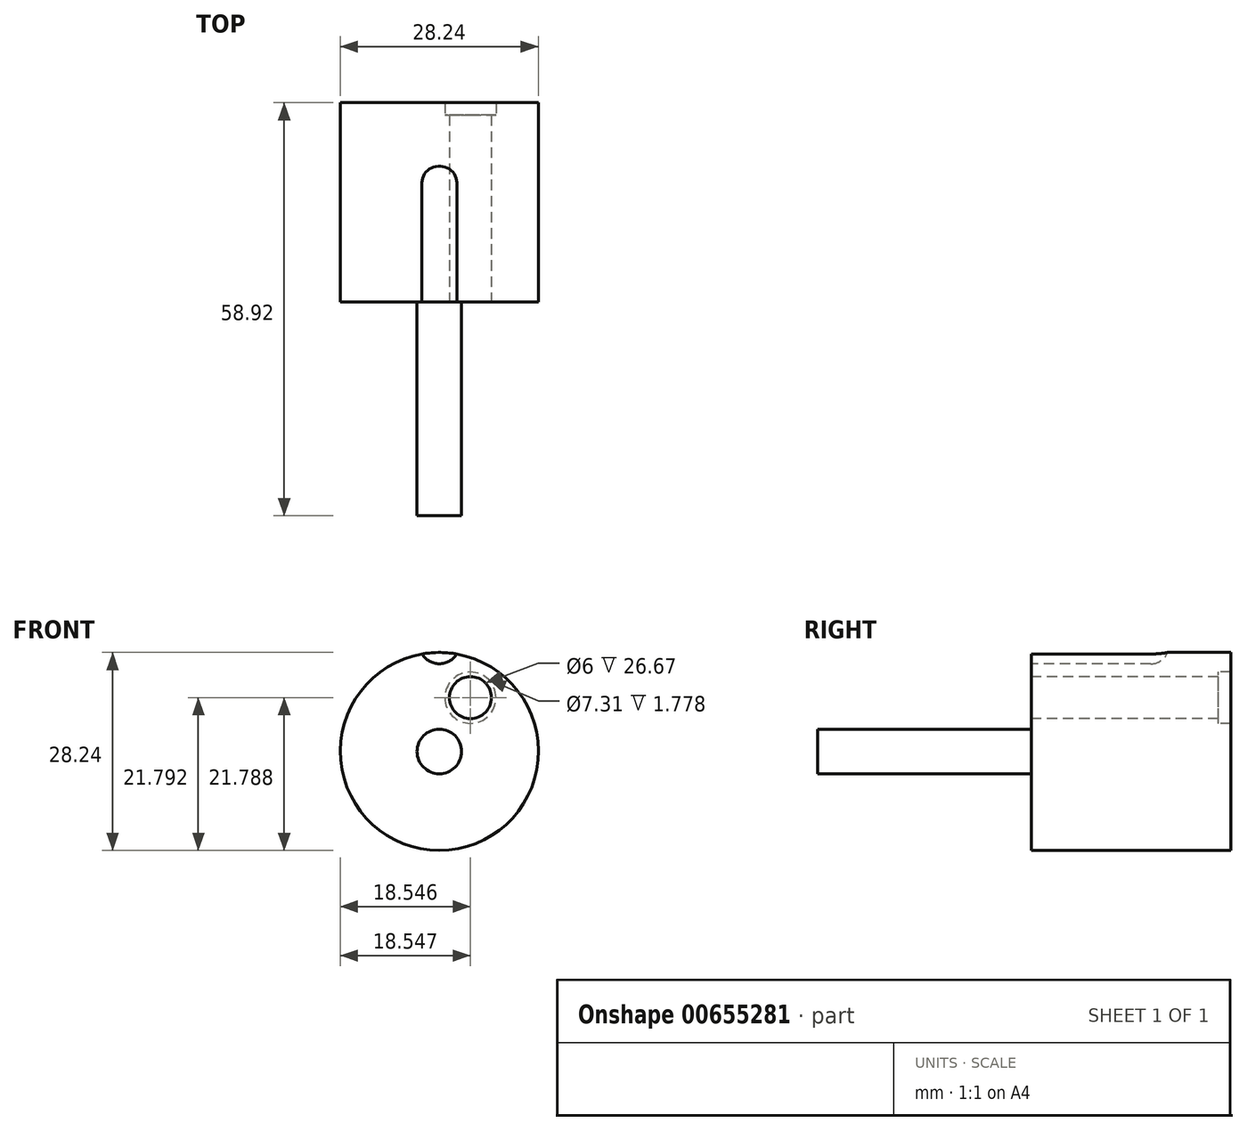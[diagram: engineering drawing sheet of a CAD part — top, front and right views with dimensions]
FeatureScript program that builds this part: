
annotation { "Feature Type Name" : "Feature", "Feature Type Description" : "" }
export const myFeature = defineFeature(function(context is Context, id is Id, definition is map)
    precondition{}
    {
        {
            var Q0;
            Q0=qCreatedBy(makeId("Front.planeOp"),FACE);
            var sketch = newSketch(context, id + "F0", { "sketchPlane" : qUnion([Q0])});
            skCircle(sketch, "E0", {"center": v(0, 0) * mm, "radius": 14.12 * mm});
            skSolve(sketch);
        }
        {
            var Q0;
            Q0=qSketchRegion(id+"F0",true);
            extrude(context, id + "F1", {"entities" : qUnion([Q0]), "endBound" : BoundingType.SYMMETRIC, "depth" : 28.45 * mm, "offsetDistance" : 25.4 * mm});
        }
        {
            var Q0;
            Q0=qCreatedBy(makeId("Front.planeOp"),FACE);
            var sketch = newSketch(context, id + "F2", { "sketchPlane" : qUnion([Q0])});
            skCircle(sketch, "E1", {"center": v(0, 0) * mm, "radius": 3.18 * mm});
            skSolve(sketch);
        }
        {
            var Q0;
            Q0=qSketchRegion(id+"F2",true);
            extrude(context, id + "F3", {"entities" : qUnion([Q0]), "operationType" : NewBodyOperationType.ADD, "depth" : 44.7 * mm, "offsetDistance" : 25.4 * mm});
        }
        {
            var Q0;
            Q0=makeQuery(id+"F1.opExtrude","CAP_FACE",FACE,{"disambiguationData":[OSD([sQuery(id+"F0.wireOp",EDGE,"E0")])],"isStart":false});
            var sketch = newSketch(context, id + "F4", { "sketchPlane" : qUnion([Q0])});
            skCircle(sketch, "E2", {"center": v(0, 15.4) * mm, "radius": 2.9 * mm});
            skSolve(sketch);
        }
        {
            var Q0;
            Q0=qSketchRegion(id+"F4",true);
            extrude(context, id + "F5", {"entities" : qUnion([Q0]), "operationType" : NewBodyOperationType.REMOVE, "oppositeDirection" : true, "depth" : 19.56 * mm, "offsetDistance" : 25.4 * mm});
        }
        {
            var Q0;
            Q0=makeQuery(id+"F5.boolean.opBoolean","COPY",EDGE,{"derivedFrom":makeQuery(id+"F5.opExtrude","CAP_EDGE",EDGE,{"disambiguationData":[OSD([sQuery(id+"F4.wireOp",EDGE,"E2")])],"isStart":false})});
            fillet(context, id + "F6", {"entities" : qUnion([Q0]), "radius" : 2.54 * mm, "tangentPropagation" : true, "allowEdgeOverflow" : false});
        }
        {
            var Q0;
            Q0=qCreatedBy(makeId("Front.planeOp"),FACE);
            var sketch = newSketch(context, id + "F7", { "sketchPlane" : qUnion([Q0])});
            skLineSegment(sketch, "E3", {"start": v(2.48, 13.9) * mm, "end": v(10.8, 9.1) * mm, "construction": true});
            skLineSegment(sketch, "E4", {"start": v(2.48, 13.9) * mm, "end": v(0, 0) * mm, "construction": true});
            skLineSegment(sketch, "E5", {"start": v(0, 0) * mm, "end": v(10.8, 9.1) * mm, "construction": true});
            skLineSegment(sketch, "E6", {"start": v(0, 0) * mm, "end": v(6.64, 11.5) * mm, "construction": true});
            skLineSegment(sketch, "E7", {"start": v(6.64, 11.5) * mm, "end": v(5.56, 9.63) * mm});
            skLineSegment(sketch, "E8", {"start": v(0, 0) * mm, "end": v(5.4, 4.55) * mm});
            skLineSegment(sketch, "E9", {"start": v(5.4, 4.55) * mm, "end": v(1.24, 6.95) * mm, "construction": true});
            skLineSegment(sketch, "E10", {"start": v(1.24, 6.95) * mm, "end": v(10.8, 9.1) * mm, "construction": true});
            skLineSegment(sketch, "E11", {"start": v(2.48, 13.9) * mm, "end": v(5.4, 4.55) * mm, "construction": true});
            skCircle(sketch, "E12", {"center": v(4.43, 7.67) * mm, "radius": 3 * mm});
            skSolve(sketch);
        }
        {
            var Q0;
            Q0=qCreatedBy(makeId("Front.planeOp"),FACE);
            var sketch = newSketch(context, id + "F8", { "sketchPlane" : qUnion([Q0])});
            skCircle(sketch, "E13", {"center": v(4.43, 7.67) * mm, "radius": 3 * mm});
            skSolve(sketch);
        }
        {
            var Q0;
            Q0=qSketchRegion(id+"F8",true);
            extrude(context, id + "F9", {"entities" : qUnion([Q0]), "operationType" : NewBodyOperationType.REMOVE, "endBound" : BoundingType.SYMMETRIC, "oppositeDirection" : true, "depth" : 45.72 * mm, "offsetDistance" : 25.4 * mm});
        }
        {
            var Q0;
            Q0=qCreatedBy(makeId("Front.planeOp"),FACE);
            cPlane(context, id + "F10", {"entities" : qUnion([Q0]), "cplaneType" : CPlaneType.OFFSET, "offset" : 12.45 * mm, "oppositeDirection" : true, "width" : 152.4 * mm, "height" : 152.4 * mm});
        }
        {
            var Q0;
            Q0=qCreatedBy(id+"F10.planeOp",FACE);
            var sketch = newSketch(context, id + "F11", { "sketchPlane" : qUnion([Q0])});
            skCircle(sketch, "E14", {"center": v(4.43, 7.67) * mm, "radius": 3.65 * mm});
            skSolve(sketch);
        }
        {
            var Q0;
            Q0=qSketchRegion(id+"F11",true);
            extrude(context, id + "F12", {"entities" : qUnion([Q0]), "operationType" : NewBodyOperationType.REMOVE, "oppositeDirection" : true, "depth" : 28.07 * mm, "offsetDistance" : 25.4 * mm});
        }
    });
